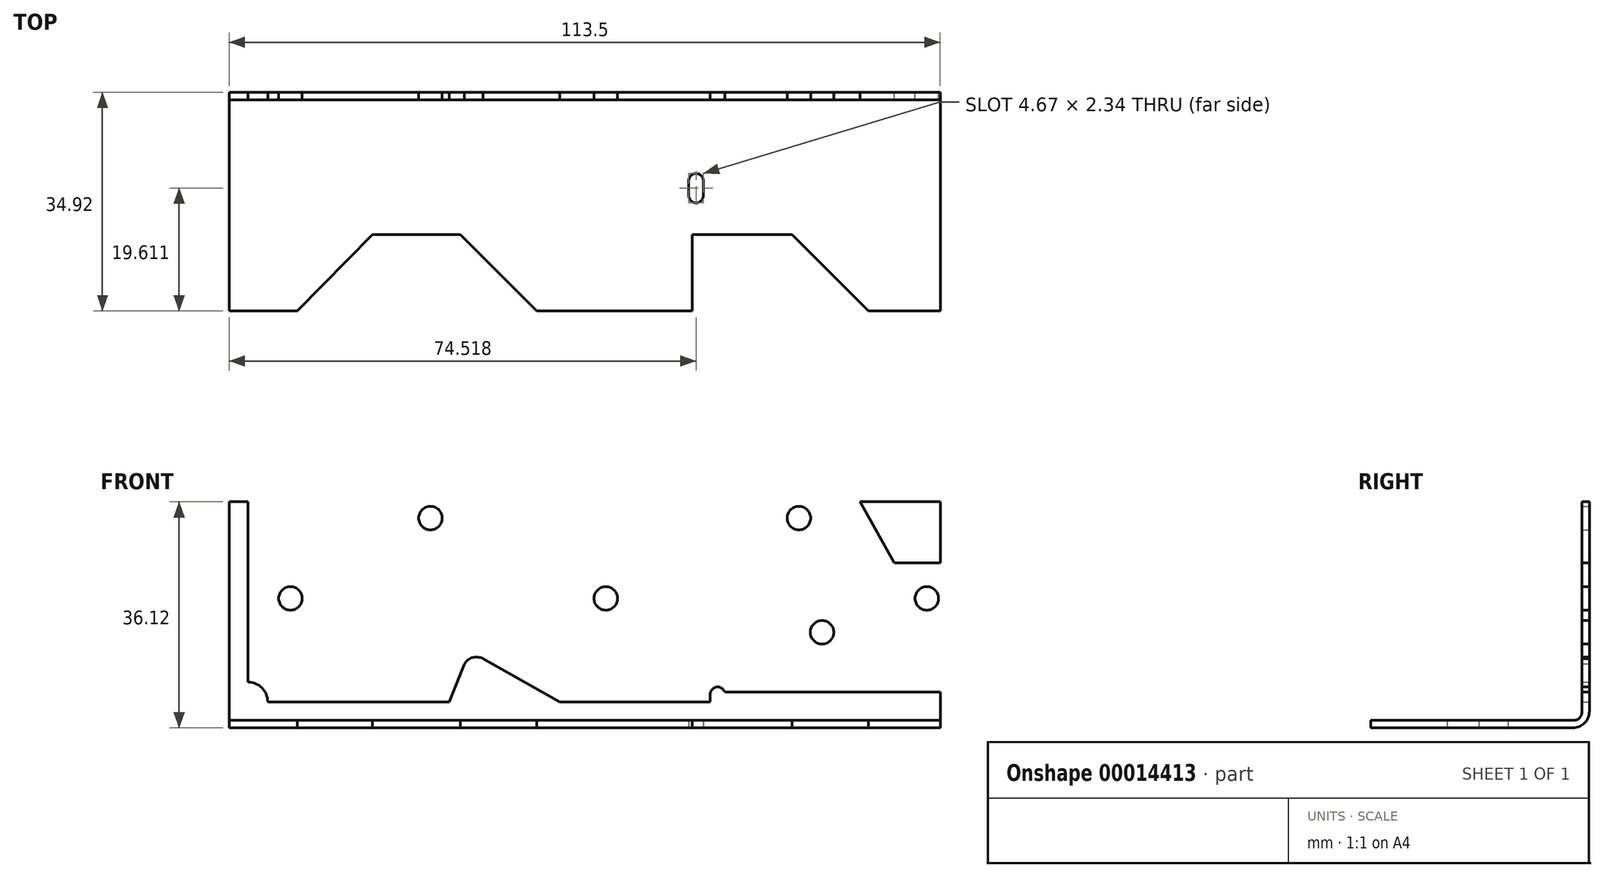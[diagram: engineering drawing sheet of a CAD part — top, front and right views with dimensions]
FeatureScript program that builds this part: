
annotation { "Feature Type Name" : "Feature", "Feature Type Description" : "" }
export const myFeature = defineFeature(function(context is Context, id is Id, definition is map)
    precondition{}
    {
        {
            var Q0;
            Q0=qCreatedBy(makeId("Right.planeOp"),FACE);
            var sketch = newSketch(context, id + "F0", { "sketchPlane" : qUnion([Q0])});
            skLineSegment(sketch, "E0", {"start": v(8.33, -9.72) * mm, "end": v(8.33, -16.87) * mm});
            skLineSegment(sketch, "E1", {"start": v(2.78, -9.72) * mm, "end": v(2.78, -16.87) * mm});
            skLineSegment(sketch, "E2", {"start": v(2.78, -9.72) * mm, "end": v(8.33, -9.72) * mm});
            skLineSegment(sketch, "E3", {"start": v(14.82, -18.06) * mm, "end": v(-17.46, -18.06) * mm});
            skLineSegment(sketch, "E4", {"start": v(14.95, -16.87) * mm, "end": v(-17.46, -16.87) * mm});
            skLineSegment(sketch, "E5", {"start": v(16.27, -15.55) * mm, "end": v(16.27, 18.06) * mm});
            skLineSegment(sketch, "E6", {"start": v(17.46, 18.06) * mm, "end": v(17.46, -15.42) * mm});
            skLineSegment(sketch, "E7", {"start": v(17.46, 18.06) * mm, "end": v(16.27, 18.06) * mm});
            skLineSegment(sketch, "E8", {"start": v(-17.46, -16.87) * mm, "end": v(-17.46, -18.06) * mm});
            skArc(sketch, "E9", {"start": v(14.95, -16.87) * mm, "mid": v(15.89, -16.48) * mm, "end": v(16.27, -15.55) * mm});
            skArc(sketch, "E10", {"start": v(14.82, -18.06) * mm, "mid": v(16.69, -17.28) * mm, "end": v(17.46, -15.42) * mm});
            skSolve(sketch);
        }
        {
            var Q0;
            Q0=qCreatedBy(makeId("Top.planeOp"),FACE);
            var Q1;
            Q1=sQuery(id+"F0.wireOp",VERTEX,"E8.end");
            cPlane(context, id + "F1", {"entities" : qUnion([Q0, Q1]), "cplaneType" : CPlaneType.PLANE_POINT, "offset" : 152.4 * mm, "width" : 152.4 * mm, "height" : 152.4 * mm});
        }
        {
            var Q0;
            Q0=qCreatedBy(id+"F1.planeOp",FACE);
            var sketch = newSketch(context, id + "F2", { "sketchPlane" : qUnion([Q0])});
            skArc(sketch, "E11", {"start": v(-55.7, 13.44) * mm, "mid": v(-53.5, 14.35) * mm, "end": v(-52.59, 16.56) * mm});
            skArc(sketch, "E12", {"start": v(53, 15) * mm, "mid": v(54.15, 13.86) * mm, "end": v(55.7, 13.44) * mm});
            skLineSegment(sketch, "E13", {"start": v(-55.7, 13.45) * mm, "end": v(-55.7, -17.72) * mm});
            skLineSegment(sketch, "E14", {"start": v(16.6, 0.99) * mm, "end": v(16.6, 3.32) * mm});
            skLineSegment(sketch, "E15", {"start": v(18.94, 3.32) * mm, "end": v(18.94, 0.99) * mm});
            skArc(sketch, "E16", {"start": v(16.6, 0.99) * mm, "mid": v(17.77, -0.19) * mm, "end": v(18.94, 0.99) * mm});
            skArc(sketch, "E17", {"start": v(18.94, 3.32) * mm, "mid": v(17.77, 4.49) * mm, "end": v(16.6, 3.32) * mm});
            skLineSegment(sketch, "E18", {"start": v(17.14, -17.72) * mm, "end": v(17.14, -5.26) * mm});
            skLineSegment(sketch, "E19", {"start": v(17.14, -5.26) * mm, "end": v(33.11, -5.26) * mm});
            skLineSegment(sketch, "E20", {"start": v(33.11, -5.26) * mm, "end": v(33.11, -5.26) * mm});
            skLineSegment(sketch, "E21", {"start": v(45.58, -17.72) * mm, "end": v(55.7, -17.72) * mm});
            skLineSegment(sketch, "E22", {"start": v(55.7, -17.72) * mm, "end": v(55.7, 13.44) * mm});
            skLineSegment(sketch, "E23", {"start": v(53, 15) * mm, "end": v(18.94, 15) * mm});
            skLineSegment(sketch, "E24", {"start": v(33.11, -5.26) * mm, "end": v(45.58, -17.72) * mm});
            skCircle(sketch, "E25", {"center": v(-49.08, -10.71) * mm, "radius": 1.84 * mm});
            skCircle(sketch, "E26", {"center": v(0.39, -10.71) * mm, "radius": 1.84 * mm});
            skCircle(sketch, "E27", {"center": v(50.25, -10.71) * mm, "radius": 1.84 * mm});
            skCircle(sketch, "E28", {"center": v(-27.27, 1.75) * mm, "radius": 1.84 * mm});
            skCircle(sketch, "E29", {"center": v(30.38, 1.75) * mm, "radius": 1.84 * mm});
            skCircle(sketch, "E30", {"center": v(45.97, 5.65) * mm, "radius": 1.84 * mm});
            skLineSegment(sketch, "E31", {"start": v(16.6, 15.39) * mm, "end": v(16.6, 16.56) * mm});
            skArc(sketch, "E32", {"start": v(16.6, 15.39) * mm, "mid": v(17.57, 14.24) * mm, "end": v(18.87, 15) * mm});
            skLineSegment(sketch, "E33", {"start": v(-7.4, -17.72) * mm, "end": v(17.14, -17.72) * mm});
            skLineSegment(sketch, "E34", {"start": v(-7.4, -17.72) * mm, "end": v(-19.87, -5.26) * mm});
            skLineSegment(sketch, "E35", {"start": v(-33.9, -5.26) * mm, "end": v(-19.87, -5.26) * mm});
            skLineSegment(sketch, "E36", {"start": v(-55.7, 17.72) * mm, "end": v(-55.7, 16.56) * mm});
            skLineSegment(sketch, "E37", {"start": v(55.7, 16.56) * mm, "end": v(-55.7, 16.56) * mm});
            skLineSegment(sketch, "E38", {"start": v(55.7, 16.56) * mm, "end": v(55.7, 17.72) * mm});
            skLineSegment(sketch, "E39", {"start": v(-19.87, 2.93) * mm, "end": v(2.34, 2.93) * mm});
            skLineSegment(sketch, "E40", {"start": v(-19.87, 8.37) * mm, "end": v(2.34, 8.37) * mm});
            skArc(sketch, "E41", {"start": v(-14.8, 5.92) * mm, "mid": v(-14.92, 5.64) * mm, "end": v(-14.8, 5.37) * mm});
            skLineSegment(sketch, "E42", {"start": v(-14.8, 5.37) * mm, "end": v(-12.36, 2.93) * mm});
            skLineSegment(sketch, "E43", {"start": v(-14.8, 5.92) * mm, "end": v(-12.35, 8.37) * mm});
            skLineSegment(sketch, "E44", {"start": v(-22.6, 5.65) * mm, "end": v(-19.87, 2.93) * mm});
            skLineSegment(sketch, "E45", {"start": v(-22.6, 5.65) * mm, "end": v(-19.87, 8.37) * mm});
            skLineSegment(sketch, "E46", {"start": v(-55.7, 17.72) * mm, "end": v(55.7, 17.72) * mm});
            skLineSegment(sketch, "E47", {"start": v(-55.7, -17.72) * mm, "end": v(-46.18, -17.72) * mm});
            skLineSegment(sketch, "E48", {"start": v(-33.9, -5.26) * mm, "end": v(-46.18, -17.72) * mm});
            skLineSegment(sketch, "E49", {"start": v(-46.18, -17.72) * mm, "end": v(-7.4, -17.72) * mm});
            skLineSegment(sketch, "E50", {"start": v(17.14, -17.72) * mm, "end": v(45.58, -17.72) * mm});
            skSolve(sketch);
        }
        {
            var Q0;
            Q0=qCreatedBy(makeId("Front.planeOp"),FACE);
            var Q1;
            Q1=sQuery(id+"F0.wireOp",VERTEX,"E6.start");
            cPlane(context, id + "F3", {"entities" : qUnion([Q0, Q1]), "cplaneType" : CPlaneType.PLANE_POINT, "offset" : 152.4 * mm, "width" : 152.4 * mm, "height" : 152.4 * mm});
        }
        {
            var Q0;
            Q0=qCreatedBy(id+"F3.planeOp",FACE);
            var sketch = newSketch(context, id + "F4", { "sketchPlane" : qUnion([Q0])});
            skArc(sketch, "E51", {"start": v(-50.62, -13.9) * mm, "mid": v(-51.55, -11.66) * mm, "end": v(-53.8, -10.73) * mm});
            skLineSegment(sketch, "E52", {"start": v(22.41, 1.18) * mm, "end": v(22.41, -1.2) * mm});
            skLineSegment(sketch, "E53", {"start": v(20.03, -1.2) * mm, "end": v(20.03, 1.18) * mm});
            skArc(sketch, "E54", {"start": v(22.41, 1.18) * mm, "mid": v(21.22, 2.37) * mm, "end": v(20.03, 1.18) * mm});
            skArc(sketch, "E55", {"start": v(20.03, -1.2) * mm, "mid": v(21.22, -2.4) * mm, "end": v(22.41, -1.2) * mm});
            skLineSegment(sketch, "E56", {"start": v(-31.57, 21.02) * mm, "end": v(-44.27, 8.32) * mm});
            skLineSegment(sketch, "E57", {"start": v(49.4, 8.32) * mm, "end": v(59.72, 8.32) * mm});
            skLineSegment(sketch, "E58", {"start": v(20.03, 8.32) * mm, "end": v(20.03, 21.02) * mm});
            skLineSegment(sketch, "E59", {"start": v(-4.58, 8.32) * mm, "end": v(20.03, 8.32) * mm});
            skLineSegment(sketch, "E60", {"start": v(-53.8, 8.32) * mm, "end": v(-44.27, 8.32) * mm});
            skLineSegment(sketch, "E61", {"start": v(59.72, 8.32) * mm, "end": v(59.72, -10.73) * mm});
            skCircle(sketch, "E62", {"center": v(-46.99, 2.61) * mm, "radius": 1.88 * mm});
            skCircle(sketch, "E63", {"center": v(3.36, 2.61) * mm, "radius": 1.88 * mm});
            skCircle(sketch, "E64", {"center": v(54.61, 2.61) * mm, "radius": 1.88 * mm});
            skCircle(sketch, "E65", {"center": v(-24.63, 15.45) * mm, "radius": 1.88 * mm});
            skCircle(sketch, "E66", {"center": v(34.19, 15.45) * mm, "radius": 1.88 * mm});
            skCircle(sketch, "E67", {"center": v(37.89, -2.8) * mm, "radius": 1.88 * mm});
            skLineSegment(sketch, "E68", {"start": v(-4.58, 8.32) * mm, "end": v(-17.28, 21.02) * mm});
            skArc(sketch, "E69", {"start": v(-16.25, -7) * mm, "mid": v(-17.92, -6.84) * mm, "end": v(-19.24, -7.9) * mm});
            skArc(sketch, "E70", {"start": v(-16.74, -8.1) * mm, "mid": v(-17.58, -8) * mm, "end": v(-18.23, -8.54) * mm});
            skLineSegment(sketch, "E71", {"start": v(-21.64, -13.9) * mm, "end": v(-19.24, -7.9) * mm});
            skLineSegment(sketch, "E72", {"start": v(-16.25, -7) * mm, "end": v(-3.99, -13.9) * mm});
            skLineSegment(sketch, "E73", {"start": v(-16.74, -8.1) * mm, "end": v(-6.83, -13.9) * mm});
            skLineSegment(sketch, "E74", {"start": v(-20.23, -13.9) * mm, "end": v(-18.23, -8.54) * mm});
            skLineSegment(sketch, "E75", {"start": v(-53.8, -15.1) * mm, "end": v(59.72, -15.1) * mm});
            skLineSegment(sketch, "E76", {"start": v(-53.8, -13.9) * mm, "end": v(59.72, -13.9) * mm});
            skLineSegment(sketch, "E77", {"start": v(-53.8, -13.9) * mm, "end": v(-53.8, -15.1) * mm});
            skLineSegment(sketch, "E78", {"start": v(59.72, -13.9) * mm, "end": v(59.72, -15.1) * mm});
            skLineSegment(sketch, "E79", {"start": v(20.03, -12.72) * mm, "end": v(20.03, -13.9) * mm});
            skLineSegment(sketch, "E80", {"start": v(22.34, -12.32) * mm, "end": v(56.97, -12.32) * mm});
            skArc(sketch, "E81", {"start": v(22.34, -12.32) * mm, "mid": v(21.02, -11.54) * mm, "end": v(20.03, -12.72) * mm});
            skArc(sketch, "E82", {"start": v(59.72, -10.73) * mm, "mid": v(58.11, -11.13) * mm, "end": v(56.97, -12.32) * mm});
            skLineSegment(sketch, "E83", {"start": v(-31.57, 21.02) * mm, "end": v(-53.8, 21.02) * mm});
            skLineSegment(sketch, "E84", {"start": v(-53.8, 8.32) * mm, "end": v(-53.8, 21.02) * mm});
            skLineSegment(sketch, "E85", {"start": v(-17.28, 21.02) * mm, "end": v(20.03, 21.02) * mm});
            skLineSegment(sketch, "E86", {"start": v(59.72, 8.32) * mm, "end": v(59.72, 21.02) * mm});
            skLineSegment(sketch, "E87", {"start": v(20.03, 21.02) * mm, "end": v(59.72, 21.02) * mm});
            skLineSegment(sketch, "E88", {"start": v(49.4, 8.32) * mm, "end": v(42.28, 21.02) * mm});
            skLineSegment(sketch, "E89", {"start": v(-53.8, 8.32) * mm, "end": v(-53.8, -10.73) * mm});
            skLineSegment(sketch, "E90", {"start": v(-31.57, 21.02) * mm, "end": v(-17.28, 21.02) * mm});
            skSolve(sketch);
        }
        {
            var Q0;
            Q0=makeQuery(id+"F0.imprint","IMPRINT",FACE,{"disambiguationData":[TD([[makeQuery(id+"F0.imprint","IMPRINT",EDGE,{"derivedFrom":sQuery(id+"F0.wireOp",EDGE,"E3")}),-1.0]])]});
            var Q1;
            Q1=qCreatedBy(id+"F1.planeOp",FACE);
            extrude(context, id + "F5", {"entities" : qUnion([Q0]), "endBoundEntityFace" : qUnion([Q1]), "depth" : 113.5 * mm, "symmetric" : true});
        }
        {
            var Q0;
            Q0=makeQuery(id+"F2.imprint","IMPRINT",FACE,{"disambiguationData":[TD([[makeQuery(id+"F2.imprint","IMPRINT",EDGE,{"derivedFrom":sQuery(id+"F2.wireOp",EDGE,"E14")}),-1.0]])]});
            var Q1;
            Q1=makeQuery(id+"F2.imprint","IMPRINT",FACE,{"disambiguationData":[TD([[makeQuery(id+"F2.imprint","IMPRINT",EDGE,{"derivedFrom":sQuery(id+"F2.wireOp",EDGE,"E29")}),-1.0]])]});
            var Q2;
            Q2=makeQuery(id+"F2.imprint","IMPRINT",FACE,{"disambiguationData":[TD([[makeQuery(id+"F2.imprint","IMPRINT",EDGE,{"derivedFrom":sQuery(id+"F2.wireOp",EDGE,"E30")}),-1.0]])]});
            var Q3;
            Q3=makeQuery(id+"F2.imprint","IMPRINT",FACE,{"disambiguationData":[TD([[makeQuery(id+"F2.imprint","IMPRINT",EDGE,{"derivedFrom":sQuery(id+"F2.wireOp",EDGE,"E27")}),-1.0]])]});
            var Q4;
            Q4=makeQuery(id+"F2.imprint","IMPRINT",FACE,{"disambiguationData":[TD([[makeQuery(id+"F2.imprint","IMPRINT",EDGE,{"derivedFrom":sQuery(id+"F2.wireOp",EDGE,"E26")}),-1.0]])]});
            var Q5;
            Q5=makeQuery(id+"F2.imprint","IMPRINT",FACE,{"disambiguationData":[TD([[makeQuery(id+"F2.imprint","IMPRINT",EDGE,{"derivedFrom":sQuery(id+"F2.wireOp",EDGE,"E28")}),-1.0]])]});
            var Q6;
            Q6=makeQuery(id+"F2.imprint","IMPRINT",FACE,{"disambiguationData":[TD([[makeQuery(id+"F2.imprint","IMPRINT",EDGE,{"derivedFrom":sQuery(id+"F2.wireOp",EDGE,"E25")}),-1.0]])]});
            var Q7;
            Q7=makeQuery(id+"F2.imprint","IMPRINT",FACE,{"disambiguationData":[TD([[makeQuery(id+"F2.imprint","IMPRINT",EDGE,{"derivedFrom":sQuery(id+"F2.wireOp",EDGE,"E18")}),-1.0]])]});
            var Q8;
            Q8=makeQuery(id+"F2.imprint","IMPRINT",FACE,{"disambiguationData":[TD([[makeQuery(id+"F2.imprint","IMPRINT",EDGE,{"derivedFrom":sQuery(id+"F2.wireOp",EDGE,"E34")}),1.0]])]});
            extrude(context, id + "F6", {"entities" : qUnion([Q0, Q1, Q2, Q3, Q4, Q5, Q6, Q7, Q8]), "operationType" : NewBodyOperationType.REMOVE, "depth" : 1.27 * mm});
        }
        {
            var Q0;
            Q0=makeQuery(id+"F4.imprint","IMPRINT",FACE,{"disambiguationData":[TD([[makeQuery(id+"F4.imprint","IMPRINT",EDGE,{"derivedFrom":sQuery(id+"F4.wireOp",EDGE,"E67")}),-1.0]])]});
            var Q1;
            Q1=makeQuery(id+"F4.imprint","IMPRINT",FACE,{"disambiguationData":[TD([[makeQuery(id+"F4.imprint","IMPRINT",EDGE,{"derivedFrom":sQuery(id+"F4.wireOp",EDGE,"E64")}),-1.0]])]});
            var Q2;
            Q2=makeQuery(id+"F4.imprint","IMPRINT",FACE,{"disambiguationData":[TD([[makeQuery(id+"F4.imprint","IMPRINT",EDGE,{"derivedFrom":sQuery(id+"F4.wireOp",EDGE,"E66")}),-1.0]])]});
            var Q3;
            Q3=makeQuery(id+"F4.imprint","IMPRINT",FACE,{"disambiguationData":[TD([[makeQuery(id+"F4.imprint","IMPRINT",EDGE,{"derivedFrom":sQuery(id+"F4.wireOp",EDGE,"E52")}),-1.0]])]});
            var Q4;
            Q4=makeQuery(id+"F4.imprint","IMPRINT",FACE,{"disambiguationData":[TD([[makeQuery(id+"F4.imprint","IMPRINT",EDGE,{"derivedFrom":sQuery(id+"F4.wireOp",EDGE,"E63")}),-1.0]])]});
            var Q5;
            Q5=makeQuery(id+"F4.imprint","IMPRINT",FACE,{"disambiguationData":[TD([[makeQuery(id+"F4.imprint","IMPRINT",EDGE,{"derivedFrom":sQuery(id+"F4.wireOp",EDGE,"E65")}),-1.0]])]});
            var Q6;
            Q6=makeQuery(id+"F4.imprint","IMPRINT",FACE,{"disambiguationData":[TD([[makeQuery(id+"F4.imprint","IMPRINT",EDGE,{"derivedFrom":sQuery(id+"F4.wireOp",EDGE,"E62")}),-1.0]])]});
            var Q7;
            Q7=makeQuery(id+"F4.imprint","IMPRINT",FACE,{"disambiguationData":[TD([[makeQuery(id+"F4.imprint","IMPRINT",EDGE,{"derivedFrom":sQuery(id+"F4.wireOp",EDGE,"E58")}),1.0]])]});
            var Q8;
            Q8=makeQuery(id+"F4.imprint","IMPRINT",FACE,{"disambiguationData":[TD([[makeQuery(id+"F4.imprint","IMPRINT",EDGE,{"derivedFrom":sQuery(id+"F4.wireOp",EDGE,"E56")}),-1.0]])]});
            extrude(context, id + "F7", {"entities" : qUnion([Q0, Q1, Q2, Q3, Q4, Q5, Q6, Q7, Q8]), "operationType" : NewBodyOperationType.REMOVE, "depth" : 1.27 * mm});
        }
    });
